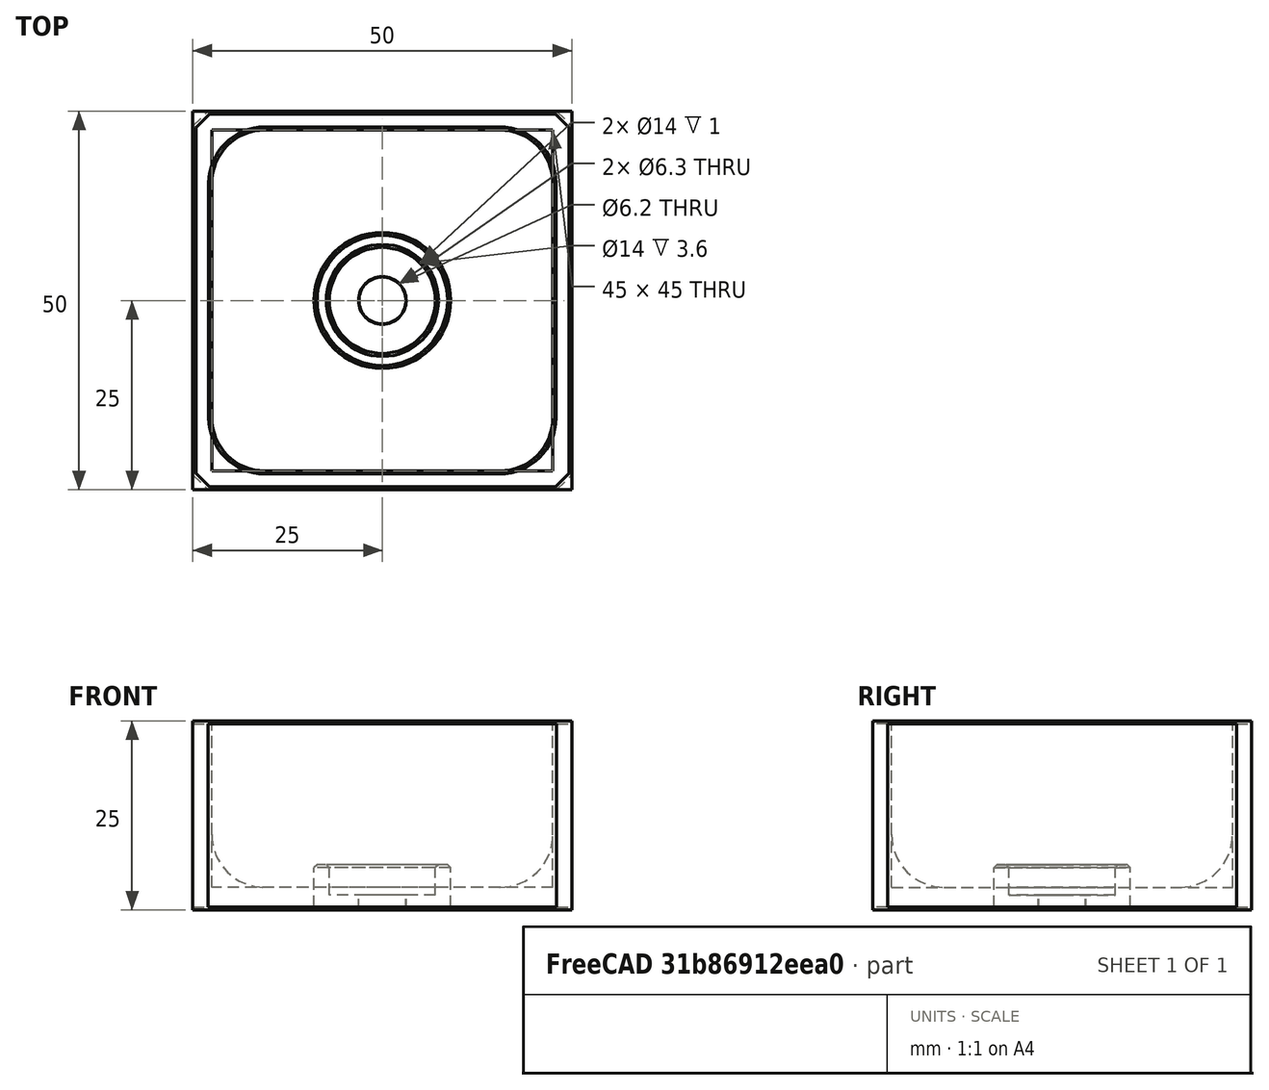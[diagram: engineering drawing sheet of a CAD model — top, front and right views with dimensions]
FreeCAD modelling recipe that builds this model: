
FCSTD DOCUMENT  (FreeCAD 0.18R14555 (Git shallow))
Label: ikea-build-pad
License: All rights reserved
LicenseURL: http://en.wikipedia.org/wiki/All_rights_reserved
objects: Part::Cylinder×5, Part::Cut×5, Part::Box×3, Part::Chamfer×3, Part::MultiFuse×1, Part::Feature×1, Part::Fillet×1
note: 19 computed .brp shape members not serialized (recipe doc carries the construction recipe); baked Part::Feature solids carry a one-line shape summary decoded from their .brp

FEATURE [Part::Box] Box  label="Cube"
  AttacherType = Attacher::AttachEngine3D
  Height = 3
  Length = 50
  Placement = pos=(-25,-25,0) rot=(0,0,1;0rad)
  Width = 50
FEATURE [Part::Cylinder] Cylinder
  Angle = 360
  AttacherType = Attacher::AttachEngine3D
  Height = 10
  Radius = 3.15
FEATURE [Part::Cylinder] Cylinder001
  Angle = 360
  AttacherType = Attacher::AttachEngine3D
  Height = 10
  Placement = pos=(0,0,2) rot=(0,0,1;0rad)
  Radius = 7
FEATURE [Part::Box] Box001  label="Cube001"
  AttacherType = Attacher::AttachEngine3D
  Height = 25
  Length = 50
  Placement = pos=(-25,-25,0) rot=(0,0,1;0rad)
  Width = 50
FEATURE [Part::Box] Box002  label="Cube002"
  AttacherType = Attacher::AttachEngine3D
  Height = 25
  Length = 45
  Placement = pos=(-22.5,-22.5,0) rot=(0,0,1;0rad)
  Width = 45
FEATURE [Part::Cut] Cut002
  Base = -> Box001
  Tool = -> Box002
FEATURE [Part::Cut] Cut
  Base = -> Box
  Tool = -> Cylinder001
FEATURE [Part::Cut] Cut003
  Base = -> Cut
  Tool = -> Cylinder
FEATURE [Part::MultiFuse] Fusion
  Shapes = -> [Cut003,Cut002]
FEATURE [Part::Feature] Fusion001
  shape: bbox 50 x 50 x 25 mm, 14 faces (baked)
FEATURE [Part::Chamfer] Chamfer
  Base = -> Fusion001
  Edges = 4 edges r=2: [Edge23,Edge24,Edge27,Edge29]
FEATURE [Part::Fillet] Fillet
  Base = -> Chamfer
  Edges = 8 edges r=7: [Edge29,Edge30,Edge31,Edge32,Edge33,Edge34,Edge35,Edge36]
FEATURE [Part::Chamfer] Chamfer001  label="tray"
  Base = -> Fillet
  Edges = 24 edges r=0.4: [Edge1,Edge2,Edge3,Edge4,Edge5,Edge6,Edge7,Edge8,Edge9,Edge10,Edge11,Edge12,Edge13,Edge14,Edge15,Edge16,Edge35,Edge36,Edge38,Edge40,Edge42,Edge44,Edge46,Edge48]
FEATURE [Part::Cylinder] Cylinder002
  Angle = 360
  AttacherType = Attacher::AttachEngine3D
  Height = 6
  Placement = pos=(0,0,2) rot=(0,0,1;0rad)
  Radius = 7
FEATURE [Part::Cylinder] Cylinder003
  Angle = 360
  AttacherType = Attacher::AttachEngine3D
  Height = 6
  Radius = 9
FEATURE [Part::Cylinder] Cylinder004
  Angle = 360
  AttacherType = Attacher::AttachEngine3D
  Height = 10
  Radius = 3.1
FEATURE [Part::Cut] Cut004
  Base = -> Cylinder003
  Tool = -> Cylinder002
FEATURE [Part::Cut] Cut005
  Base = -> Cut004
  Tool = -> Cylinder004
FEATURE [Part::Chamfer] Chamfer002
  Base = -> Cut005
  Edges = 3 edges r=0.4: [Edge1,Edge3,Edge4]
